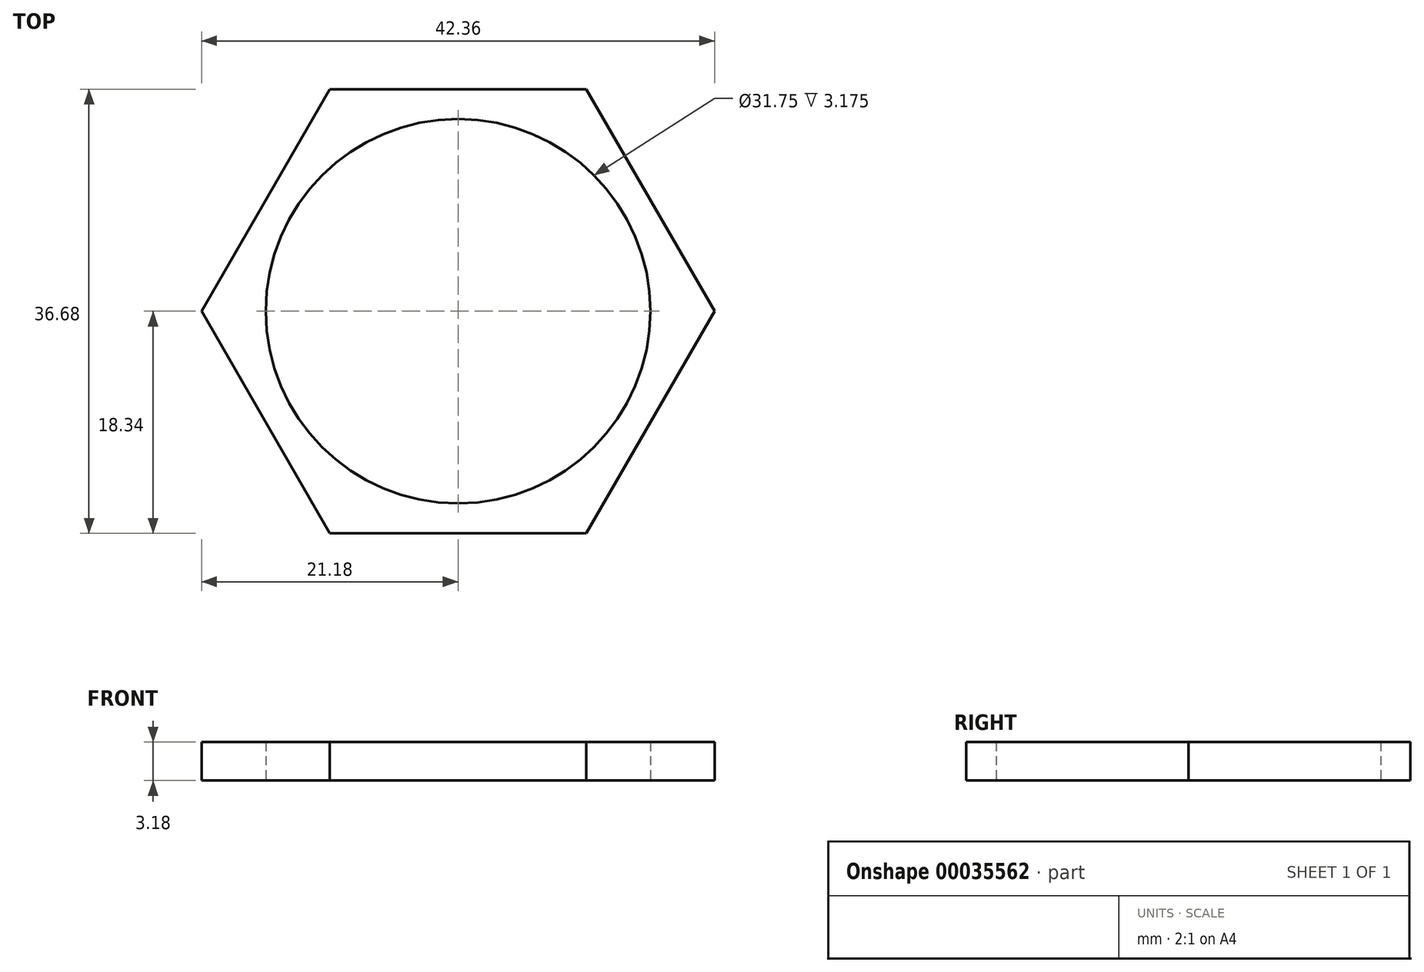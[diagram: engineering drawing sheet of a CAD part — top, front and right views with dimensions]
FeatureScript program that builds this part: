
annotation { "Feature Type Name" : "Feature", "Feature Type Description" : "" }
export const myFeature = defineFeature(function(context is Context, id is Id, definition is map)
    precondition{}
    {
        {
            var Q0;
            Q0=qCreatedBy(makeId("Top.planeOp"),FACE);
            var sketch = newSketch(context, id + "F0", { "sketchPlane" : qUnion([Q0])});
            skCircle(sketch, "E0", {"center": v(0, 0) * mm, "radius": 15.88 * mm});
            skCircle(sketch, "E1.cCircle", {"center": v(0, 0) * mm, "radius": 18.34 * mm, "construction": true});
            skLineSegment(sketch, "E1.0", {"start": v(-10.59, 18.34) * mm, "end": v(10.59, 18.34) * mm});
            skLineSegment(sketch, "E1.1", {"start": v(10.59, 18.34) * mm, "end": v(21.18, 0) * mm});
            skLineSegment(sketch, "E1.2", {"start": v(21.18, 0) * mm, "end": v(10.59, -18.34) * mm});
            skLineSegment(sketch, "E1.3", {"start": v(10.59, -18.34) * mm, "end": v(-10.59, -18.34) * mm});
            skLineSegment(sketch, "E1.4", {"start": v(-10.59, -18.34) * mm, "end": v(-21.18, 0) * mm});
            skLineSegment(sketch, "E1.5", {"start": v(-21.18, 0) * mm, "end": v(-10.59, 18.34) * mm});
            skPoint(sketch, "E1.0.midPoint", {"position": v(0, 18.34) * mm});
            skSolve(sketch);
        }
        {
            var Q0;
            Q0 = qSketchRegion(id + "F0", true);
            extrude(context, id + "F1", {"entities" : qUnion([Q0]), "depth" : 3.17 * mm});
        }
    });
